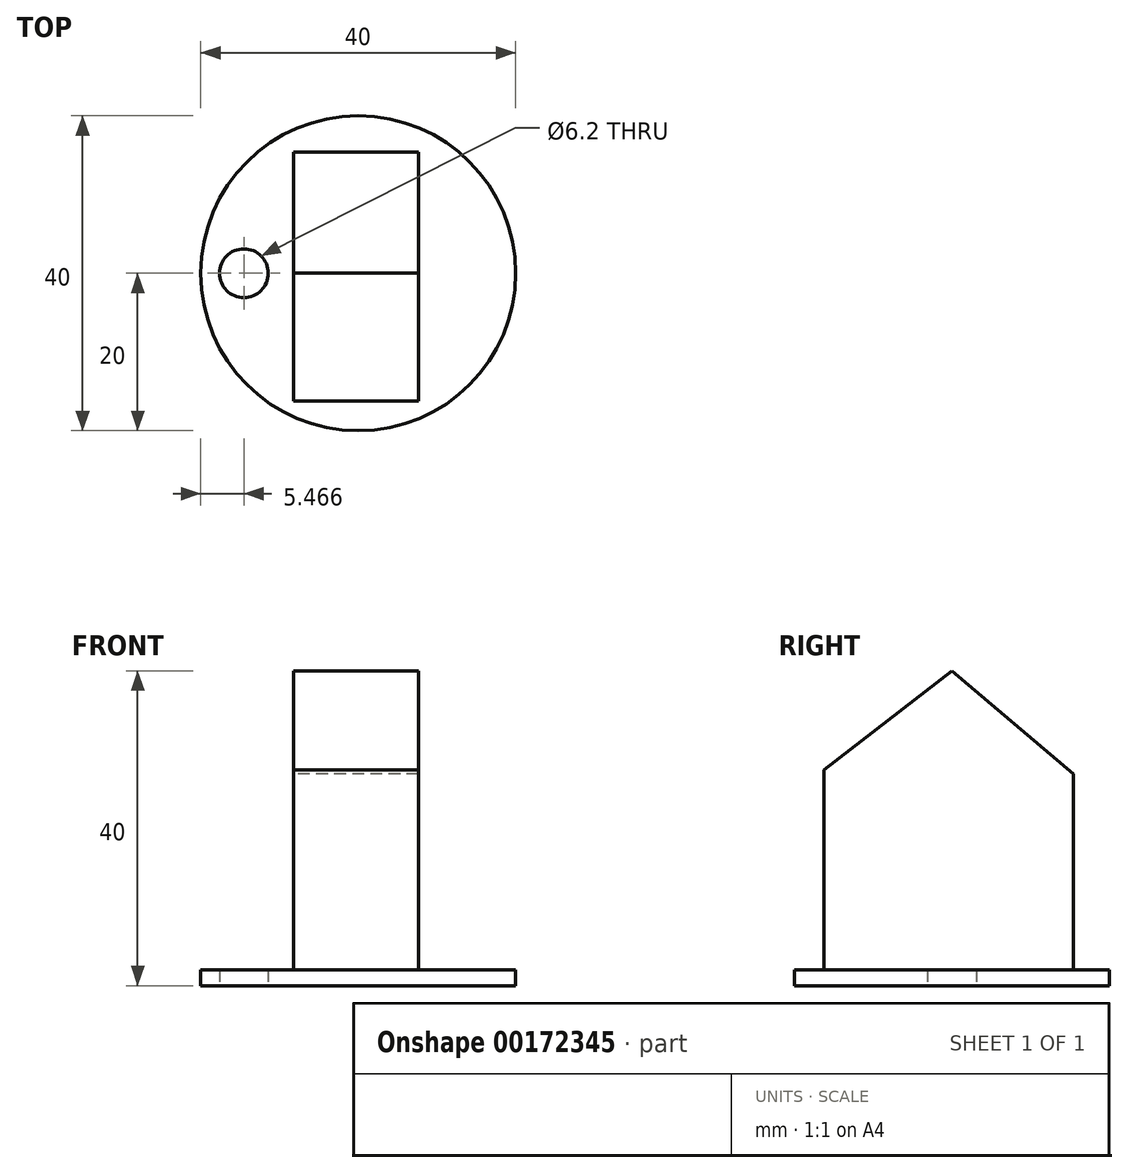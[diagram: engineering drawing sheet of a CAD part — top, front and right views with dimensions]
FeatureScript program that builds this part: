
annotation { "Feature Type Name" : "Feature", "Feature Type Description" : "" }
export const myFeature = defineFeature(function(context is Context, id is Id, definition is map)
    precondition{}
    {
        {
            var Q0;
            Q0=qCreatedBy(makeId("Top.planeOp"),FACE);
            var sketch = newSketch(context, id + "F0", { "sketchPlane" : qUnion([Q0])});
            skCircle(sketch, "E0", {"center": v(0, 0) * mm, "radius": 20 * mm});
            skLineSegment(sketch, "E1.bottom", {"start": v(7.64, 15.42) * mm, "end": v(-8.19, 15.42) * mm});
            skLineSegment(sketch, "E1.top", {"start": v(7.64, -16.24) * mm, "end": v(-8.19, -16.24) * mm});
            skLineSegment(sketch, "E1.left", {"start": v(7.64, 15.42) * mm, "end": v(7.64, -16.24) * mm});
            skLineSegment(sketch, "E1.right", {"start": v(-8.19, 15.42) * mm, "end": v(-8.19, -16.24) * mm});
            skCircle(sketch, "E2", {"center": v(-14.53, 0) * mm, "radius": 3.1 * mm});
            skSolve(sketch);
        }
        {
            var Q0;
            Q0 = qSketchRegion(id + "F0", true);
            extrude(context, id + "F1", {"entities" : qUnion([Q0]), "depth" : 2 * mm});
        }
        {
            var Q0;
            Q0=makeQuery(id+"F0.imprint","IMPRINT",FACE,{"disambiguationData":[TD([[makeQuery(id+"F0.imprint","IMPRINT",EDGE,{"derivedFrom":sQuery(id+"F0.wireOp",EDGE,"E1.bottom")}),1.0]])]});
            extrude(context, id + "F2", {"entities" : qUnion([Q0]), "operationType" : NewBodyOperationType.ADD, "depth" : 40 * mm});
        }
        {
            var Q0;
            Q0=makeQuery(id+"F2.opExtrude","SWEPT_FACE",FACE,{"disambiguationData":[OSD([sQuery(id+"F0.wireOp",EDGE,"E1.right")])]});
            var sketch = newSketch(context, id + "F3", { "sketchPlane" : qUnion([Q0])});
            skLineSegment(sketch, "E3", {"start": v(16.24, 27.43) * mm, "end": v(0, 40) * mm});
            skLineSegment(sketch, "E4", {"start": v(0, 40) * mm, "end": v(-15.42, 26.89) * mm});
            skSolve(sketch);
        }
        {
            var Q0;
            {var subQ0=sQuery(id+"F3.wireOp",EDGE,"E3");Q0=makeQuery(id+"F3.imprint","IMPRINT",FACE,{"disambiguationData":[TD([[makeQuery(id+"F3.imprint","IMPRINT",EDGE,{"derivedFrom":subQ0}),-1.0]])]});}
            var Q1;
            {var subQ0=sQuery(id+"F3.wireOp",EDGE,"E4");Q1=makeQuery(id+"F3.imprint","IMPRINT",FACE,{"disambiguationData":[TD([[makeQuery(id+"F3.imprint","IMPRINT",EDGE,{"derivedFrom":subQ0}),-1.0]])]});}
            extrude(context, id + "F4", {"entities" : qUnion([Q0, Q1]), "operationType" : NewBodyOperationType.REMOVE, "oppositeDirection" : true, "depth" : 25 * mm});
        }
    });
